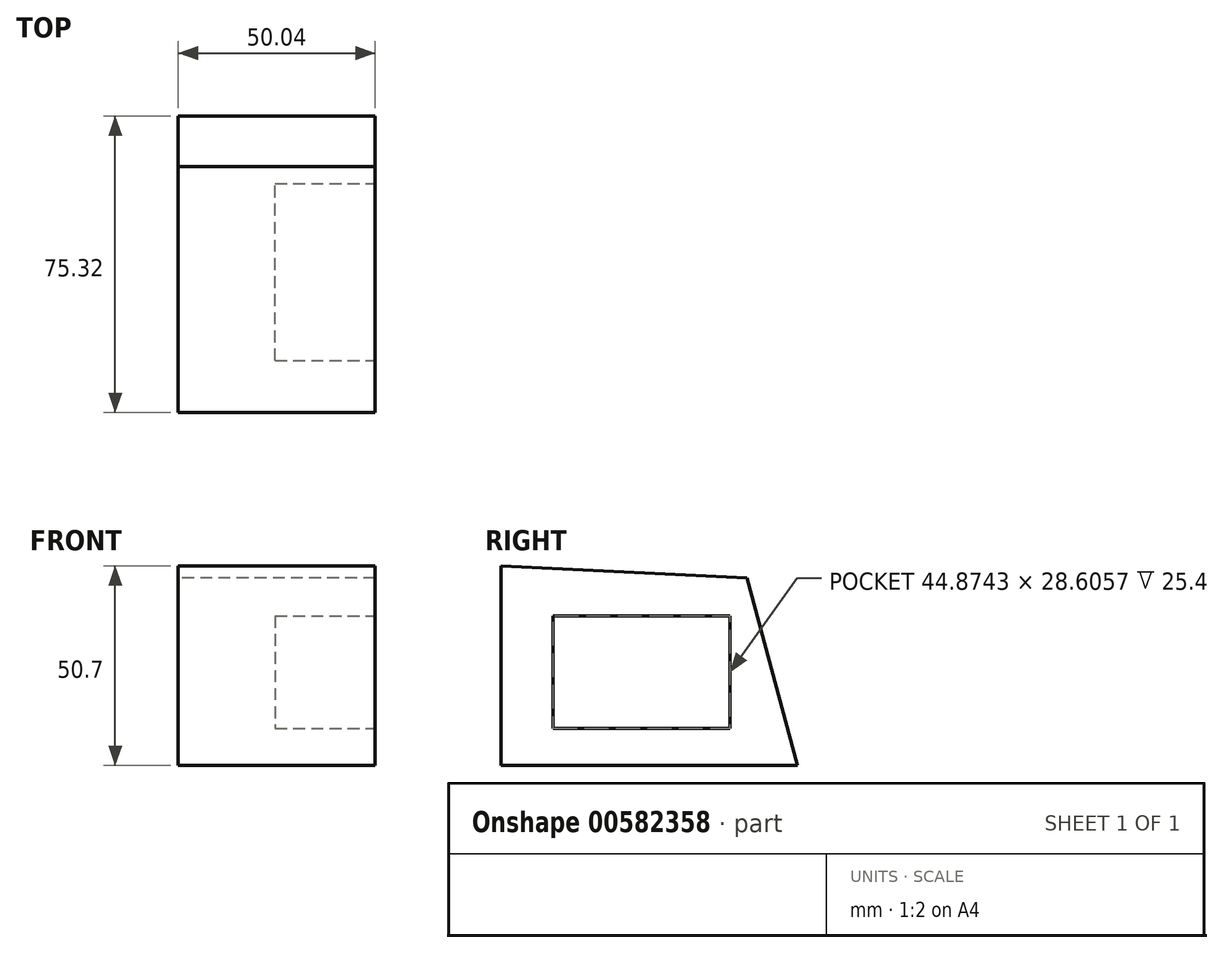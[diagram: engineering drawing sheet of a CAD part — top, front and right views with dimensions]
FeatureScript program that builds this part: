
annotation { "Feature Type Name" : "Feature", "Feature Type Description" : "" }
export const myFeature = defineFeature(function(context is Context, id is Id, definition is map)
    precondition{}
    {
        {
            var Q0;
            Q0=qCreatedBy(makeId("Right.planeOp"),FACE);
            var sketch = newSketch(context, id + "F0", { "sketchPlane" : qUnion([Q0])});
            skLineSegment(sketch, "E0", {"start": v(-5.08, 0) * mm, "end": v(-80.4, 0) * mm});
            skLineSegment(sketch, "E1", {"start": v(-80.4, 0) * mm, "end": v(-80.4, 50.7) * mm});
            skLineSegment(sketch, "E2", {"start": v(-80.4, 50.7) * mm, "end": v(-17.9, 47.66) * mm});
            skLineSegment(sketch, "E3", {"start": v(-17.9, 47.66) * mm, "end": v(-5.08, 0) * mm});
            skSolve(sketch);
        }
        {
            var Q0;
            Q0=makeQuery(id+"F0.imprint","IMPRINT",FACE,{"disambiguationData":[TD([[makeQuery(id+"F0.imprint","IMPRINT",EDGE,{"derivedFrom":sQuery(id+"F0.wireOp",EDGE,"E0")}),-1.0]])]});
            extrude(context, id + "F1", {"entities" : qUnion([Q0]), "depth" : 50.04 * mm, "offsetDistance" : 25.4 * mm});
        }
        {
            var Q0;
            Q0=makeQuery(id+"F1.opExtrude","CAP_FACE",FACE,{"disambiguationData":[OSD([sQuery(id+"F0.wireOp",EDGE,"E0"),sQuery(id+"F0.wireOp",EDGE,"E1"),sQuery(id+"F0.wireOp",EDGE,"E2"),sQuery(id+"F0.wireOp",EDGE,"E3")])],"isStart":false});
            var sketch = newSketch(context, id + "F2", { "sketchPlane" : qUnion([Q0])});
            skSolve(sketch);
        }
        {
            var Q0;
            Q0=makeQuery(id+"F2.imprint","IMPRINT",FACE,{"disambiguationData":[TD([[makeQuery(id+"F2.imprint","IMPRINT",EDGE,{"derivedFrom":makeQuery(id+"F1.opExtrude","CAP_EDGE",EDGE,{"disambiguationData":[OSD([sQuery(id+"F0.wireOp",EDGE,"E0")])],"isStart":false})}),-1.0]])]});
            var sketch = newSketch(context, id + "F3", { "sketchPlane" : qUnion([Q0])});
            skLineSegment(sketch, "E4.bottom", {"start": v(-67.17, 38) * mm, "end": v(-22.3, 38) * mm});
            skLineSegment(sketch, "E4.top", {"start": v(-67.17, 9.4) * mm, "end": v(-22.3, 9.4) * mm});
            skLineSegment(sketch, "E4.left", {"start": v(-67.17, 38) * mm, "end": v(-67.17, 9.4) * mm});
            skLineSegment(sketch, "E4.right", {"start": v(-22.3, 38) * mm, "end": v(-22.3, 9.4) * mm});
            skSolve(sketch);
        }
        {
            var Q0;
            Q0=makeQuery(id+"F3.imprint","IMPRINT",FACE,{"disambiguationData":[TD([[makeQuery(id+"F3.imprint","IMPRINT",EDGE,{"derivedFrom":sQuery(id+"F3.wireOp",EDGE,"E4.bottom")}),-1.0]])]});
            extrude(context, id + "F4", {"entities" : qUnion([Q0]), "operationType" : NewBodyOperationType.REMOVE, "oppositeDirection" : true, "depth" : 25.4 * mm, "offsetDistance" : 25.4 * mm});
        }
    });
